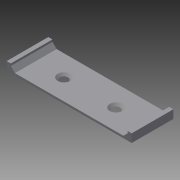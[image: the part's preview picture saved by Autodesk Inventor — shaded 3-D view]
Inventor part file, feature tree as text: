
AUTODESK INVENTOR PART (.ipt)
format: ipt  version: 2015 (Build 190159000, 159)  size: 102,912 bytes
history: native  units: mm
features: sketch x3, extrude x2, hole x1, chamfer x1
ambient origin geometry x8: Origin, YZ Plane, XZ Plane, XY Plane, X Axis, Y Axis, Z Axis, Center Point
bodies: Solid1 (feature_tree)
feature tree (7):
  extrude  "Extrusion1"  Depth=20.0mm
  hole  "Hole1"  [1 undecoded]
  extrude  "Extrusion2"  Depth=10.0mm
  chamfer  "Chamfer1"  Distance=10.0mm
  sketch  "Sketch1"  dims[d0=60.0mm d1=20.0mm]
  sketch  "Sketch2"  dims[d2=1.0mm d3=0.0mm d4=25.0mm]
  sketch  "Sketch3"  dims[d5=17.5mm d6=10.0mm d7=10.0mm d8=17.5mm d9=3.0mm d10=6.0mm d11=6.0mm d12=2.0mm d13=90.0deg d14=8.0mm d15=20.594885mm d16=2.0mm d17=2.0mm d18=3.0mm d19=0.0mm d20=2.0mm d21=2.0mm d22=45.0deg]
note: 1 required parameter value undecoded (feature->parameter linkage not recoverable at this tier; creation-order binding heuristic only, values carry confidence <= 0.55)
